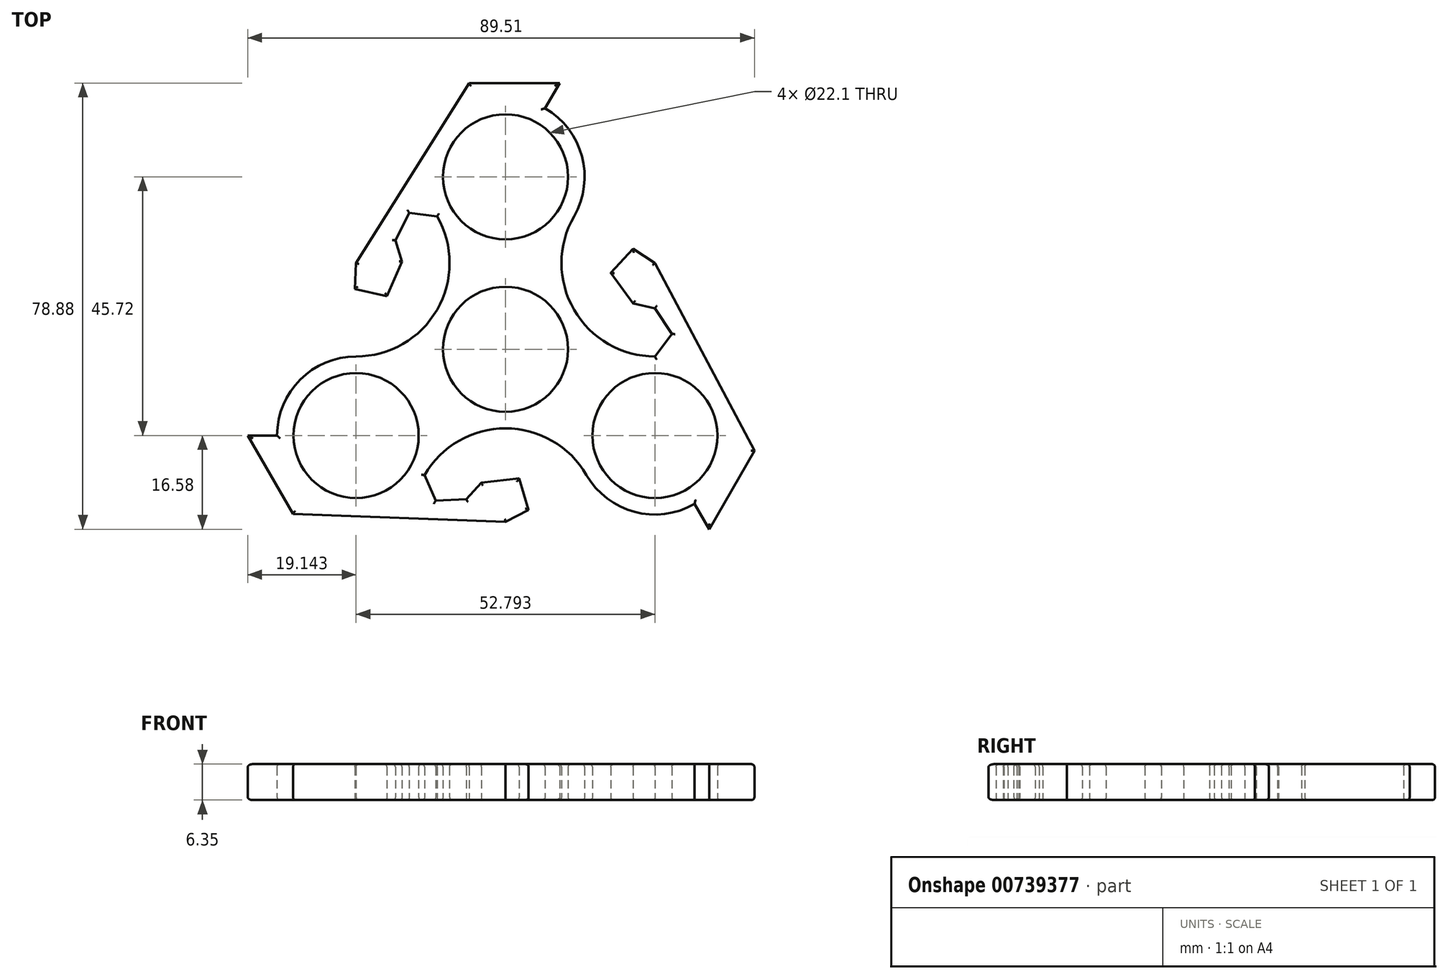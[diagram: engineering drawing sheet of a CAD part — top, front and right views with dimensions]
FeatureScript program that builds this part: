
annotation { "Feature Type Name" : "Feature", "Feature Type Description" : "" }
export const myFeature = defineFeature(function(context is Context, id is Id, definition is map)
    precondition{}
    {
        {
            var Q0;
            Q0=qCreatedBy(makeId("Top.planeOp"),FACE);
            var sketch = newSketch(context, id + "F0", { "sketchPlane" : qUnion([Q0])});
            skCircle(sketch, "E0", {"center": v(0, 0) * mm, "radius": 11.05 * mm});
            skCircle(sketch, "E1", {"center": v(0, 0) * mm, "radius": 13.97 * mm});
            skLineSegment(sketch, "E2", {"start": v(0, 0) * mm, "end": v(0, 30.48) * mm});
            skCircle(sketch, "E3", {"center": v(0, 30.48) * mm, "radius": 11.05 * mm});
            skCircle(sketch, "E4", {"center": v(0, 30.48) * mm, "radius": 13.97 * mm});
            skCircle(sketch, "E5.1.0", {"center": v(-26.4, -15.24) * mm, "radius": 13.97 * mm});
            skCircle(sketch, "E5.1.1", {"center": v(-26.4, -15.24) * mm, "radius": 11.05 * mm});
            skCircle(sketch, "E5.2.0", {"center": v(26.4, -15.24) * mm, "radius": 13.97 * mm});
            skCircle(sketch, "E5.2.1", {"center": v(26.4, -15.24) * mm, "radius": 11.05 * mm});
            skArc(sketch, "E6", {"start": v(-26.4, -1.27) * mm, "mid": v(-12.1, 6.98) * mm, "end": v(-12.1, 23.5) * mm});
            skArc(sketch, "E7.1.0", {"start": v(14.3, -22.23) * mm, "mid": v(0, -13.97) * mm, "end": v(-14.3, -22.23) * mm});
            skArc(sketch, "E7.2.0", {"start": v(12.1, 23.5) * mm, "mid": v(12.1, 6.98) * mm, "end": v(26.4, -1.27) * mm});
            skLineSegment(sketch, "E8", {"start": v(-34.35, -25.15) * mm, "end": v(-37.52, -29.1) * mm});
            skLineSegment(sketch, "E9", {"start": v(-37.52, -29.1) * mm, "end": v(-45.54, -15.24) * mm});
            skLineSegment(sketch, "E10", {"start": v(-45.54, -15.24) * mm, "end": v(-26.4, -15.24) * mm});
            skLineSegment(sketch, "E11", {"start": v(-37.52, -29.1) * mm, "end": v(0, -30.48) * mm});
            skLineSegment(sketch, "E12.1.0", {"start": v(35.97, -31.82) * mm, "end": v(26.4, -15.24) * mm});
            skLineSegment(sketch, "E12.1.1", {"start": v(43.97, -17.94) * mm, "end": v(35.97, -31.82) * mm});
            skLineSegment(sketch, "E12.1.2", {"start": v(43.97, -17.94) * mm, "end": v(26.4, 15.24) * mm});
            skLineSegment(sketch, "E12.2.0", {"start": v(9.57, 47.06) * mm, "end": v(0, 30.48) * mm});
            skLineSegment(sketch, "E12.2.1", {"start": v(-6.45, 47.05) * mm, "end": v(9.57, 47.06) * mm});
            skPoint(sketch, "E13", {"position": v(22.56, 17.73) * mm});
            skPoint(sketch, "E14", {"position": v(18.58, 13.48) * mm});
            skPoint(sketch, "E15", {"position": v(22.56, 8.09) * mm});
            skPoint(sketch, "E16", {"position": v(26.4, 7.23) * mm});
            skPoint(sketch, "E17", {"position": v(29.37, 2.7) * mm});
            skLineSegment(sketch, "E18", {"start": v(26.4, 15.24) * mm, "end": v(22.56, 17.73) * mm});
            skLineSegment(sketch, "E19", {"start": v(22.56, 17.73) * mm, "end": v(18.58, 13.48) * mm});
            skLineSegment(sketch, "E20", {"start": v(18.58, 13.48) * mm, "end": v(22.56, 8.09) * mm});
            skLineSegment(sketch, "E21", {"start": v(22.56, 8.09) * mm, "end": v(26.4, 7.23) * mm});
            skLineSegment(sketch, "E22", {"start": v(26.4, 7.23) * mm, "end": v(29.37, 2.7) * mm});
            skLineSegment(sketch, "E23", {"start": v(29.37, 2.7) * mm, "end": v(26.4, -1.27) * mm});
            skLineSegment(sketch, "E24.1.0", {"start": v(-26.4, 15.24) * mm, "end": v(-26.63, 10.67) * mm});
            skPoint(sketch, "E24.1.1", {"position": v(-20.96, 9.36) * mm});
            skLineSegment(sketch, "E24.1.2", {"start": v(-26.63, 10.67) * mm, "end": v(-20.96, 9.36) * mm});
            skPoint(sketch, "E24.1.3", {"position": v(-18.28, 15.5) * mm});
            skLineSegment(sketch, "E24.1.4", {"start": v(-20.96, 9.36) * mm, "end": v(-18.28, 15.5) * mm});
            skLineSegment(sketch, "E24.1.5", {"start": v(-19.46, 19.24) * mm, "end": v(-17.02, 24.08) * mm});
            skPoint(sketch, "E24.1.7", {"position": v(-17.02, 24.08) * mm});
            skLineSegment(sketch, "E24.1.8", {"start": v(-17.02, 24.08) * mm, "end": v(-12.1, 23.5) * mm});
            skLineSegment(sketch, "E24.2.0", {"start": v(0, -30.48) * mm, "end": v(4.08, -28.4) * mm});
            skPoint(sketch, "E24.2.1", {"position": v(2.38, -22.83) * mm});
            skLineSegment(sketch, "E24.2.2", {"start": v(4.08, -28.4) * mm, "end": v(2.38, -22.83) * mm});
            skPoint(sketch, "E24.2.3", {"position": v(-4.28, -23.58) * mm});
            skLineSegment(sketch, "E24.2.4", {"start": v(2.38, -22.83) * mm, "end": v(-4.28, -23.58) * mm});
            skLineSegment(sketch, "E24.2.5", {"start": v(-6.93, -26.48) * mm, "end": v(-12.35, -26.78) * mm});
            skPoint(sketch, "E24.2.6", {"position": v(-6.93, -26.48) * mm});
            skPoint(sketch, "E24.2.7", {"position": v(-12.35, -26.78) * mm});
            skLineSegment(sketch, "E24.2.8", {"start": v(-12.35, -26.78) * mm, "end": v(-14.3, -22.22) * mm});
            skLineSegment(sketch, "E25", {"start": v(-18.28, 15.5) * mm, "end": v(-19.46, 19.24) * mm});
            skLineSegment(sketch, "E26", {"start": v(-4.28, -23.58) * mm, "end": v(-6.93, -26.48) * mm});
            skLineSegment(sketch, "E27", {"start": v(-6.45, 47.05) * mm, "end": v(-26.4, 15.24) * mm});
            skSolve(sketch);
        }
        {
            var Q0;
            Q0 = qSketchRegion(id + "F0", true);
            extrude(context, id + "F1", {"entities" : qUnion([Q0]), "depth" : 6.35 * mm, "offsetDistance" : 25.4 * mm});
        }
        {
            var Q0;
            Q0=makeQuery(id+"F1.opExtrude","CAP_FACE",FACE,{"disambiguationData":[OSD([sQuery(id+"F0.wireOp",EDGE,"E0"),sQuery(id+"F0.wireOp",EDGE,"E3"),sQuery(id+"F0.wireOp",EDGE,"E4"),sQuery(id+"F0.wireOp",EDGE,"E5.1.0"),sQuery(id+"F0.wireOp",EDGE,"E5.1.1"),sQuery(id+"F0.wireOp",EDGE,"E5.2.0"),sQuery(id+"F0.wireOp",EDGE,"E5.2.1"),sQuery(id+"F0.wireOp",EDGE,"E6"),sQuery(id+"F0.wireOp",EDGE,"E7.1.0"),sQuery(id+"F0.wireOp",EDGE,"E7.2.0"),sQuery(id+"F0.wireOp",EDGE,"E9"),sQuery(id+"F0.wireOp",EDGE,"E10"),sQuery(id+"F0.wireOp",EDGE,"E11"),sQuery(id+"F0.wireOp",EDGE,"E12.1.0"),sQuery(id+"F0.wireOp",EDGE,"E12.1.1"),sQuery(id+"F0.wireOp",EDGE,"E12.1.2"),sQuery(id+"F0.wireOp",EDGE,"E12.2.0"),sQuery(id+"F0.wireOp",EDGE,"E12.2.1"),sQuery(id+"F0.wireOp",EDGE,"E18"),sQuery(id+"F0.wireOp",EDGE,"E19"),sQuery(id+"F0.wireOp",EDGE,"E20"),sQuery(id+"F0.wireOp",EDGE,"E21"),sQuery(id+"F0.wireOp",EDGE,"E22"),sQuery(id+"F0.wireOp",EDGE,"E23"),sQuery(id+"F0.wireOp",EDGE,"E24.1.0"),sQuery(id+"F0.wireOp",EDGE,"E24.1.2"),sQuery(id+"F0.wireOp",EDGE,"E24.1.4"),sQuery(id+"F0.wireOp",EDGE,"E24.1.5"),sQuery(id+"F0.wireOp",EDGE,"E24.1.8"),sQuery(id+"F0.wireOp",EDGE,"E24.2.0"),sQuery(id+"F0.wireOp",EDGE,"E24.2.2"),sQuery(id+"F0.wireOp",EDGE,"E24.2.4"),sQuery(id+"F0.wireOp",EDGE,"E24.2.5"),sQuery(id+"F0.wireOp",EDGE,"E24.2.8"),sQuery(id+"F0.wireOp",EDGE,"E25"),sQuery(id+"F0.wireOp",EDGE,"E26"),sQuery(id+"F0.wireOp",EDGE,"E27")])],"isStart":false});
            var Q1;
            Q1=makeQuery(id+"F1.opExtrude","CAP_FACE",FACE,{"disambiguationData":[OSD([sQuery(id+"F0.wireOp",EDGE,"E0"),sQuery(id+"F0.wireOp",EDGE,"E3"),sQuery(id+"F0.wireOp",EDGE,"E4"),sQuery(id+"F0.wireOp",EDGE,"E5.1.0"),sQuery(id+"F0.wireOp",EDGE,"E5.1.1"),sQuery(id+"F0.wireOp",EDGE,"E5.2.0"),sQuery(id+"F0.wireOp",EDGE,"E5.2.1"),sQuery(id+"F0.wireOp",EDGE,"E6"),sQuery(id+"F0.wireOp",EDGE,"E7.1.0"),sQuery(id+"F0.wireOp",EDGE,"E7.2.0"),sQuery(id+"F0.wireOp",EDGE,"E9"),sQuery(id+"F0.wireOp",EDGE,"E10"),sQuery(id+"F0.wireOp",EDGE,"E11"),sQuery(id+"F0.wireOp",EDGE,"E12.1.0"),sQuery(id+"F0.wireOp",EDGE,"E12.1.1"),sQuery(id+"F0.wireOp",EDGE,"E12.1.2"),sQuery(id+"F0.wireOp",EDGE,"E12.2.0"),sQuery(id+"F0.wireOp",EDGE,"E12.2.1"),sQuery(id+"F0.wireOp",EDGE,"E18"),sQuery(id+"F0.wireOp",EDGE,"E19"),sQuery(id+"F0.wireOp",EDGE,"E20"),sQuery(id+"F0.wireOp",EDGE,"E21"),sQuery(id+"F0.wireOp",EDGE,"E22"),sQuery(id+"F0.wireOp",EDGE,"E23"),sQuery(id+"F0.wireOp",EDGE,"E24.1.0"),sQuery(id+"F0.wireOp",EDGE,"E24.1.2"),sQuery(id+"F0.wireOp",EDGE,"E24.1.4"),sQuery(id+"F0.wireOp",EDGE,"E24.1.5"),sQuery(id+"F0.wireOp",EDGE,"E24.1.8"),sQuery(id+"F0.wireOp",EDGE,"E24.2.0"),sQuery(id+"F0.wireOp",EDGE,"E24.2.2"),sQuery(id+"F0.wireOp",EDGE,"E24.2.4"),sQuery(id+"F0.wireOp",EDGE,"E24.2.5"),sQuery(id+"F0.wireOp",EDGE,"E24.2.8"),sQuery(id+"F0.wireOp",EDGE,"E25"),sQuery(id+"F0.wireOp",EDGE,"E26"),sQuery(id+"F0.wireOp",EDGE,"E27")])],"isStart":true});
            fillet(context, id + "F2", {"entities" : qUnion([Q0, Q1]), "radius" : 0.5 * mm, "tangentPropagation" : true, "allowEdgeOverflow" : false});
        }
    });
